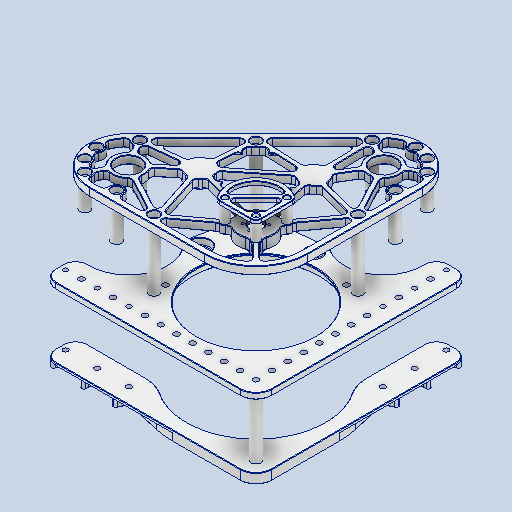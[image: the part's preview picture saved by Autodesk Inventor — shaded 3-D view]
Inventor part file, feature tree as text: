
AUTODESK INVENTOR PART (.ipt)
format: ipt  version: 2024 (Build 280153000, 153)  size: 1,680,896 bytes
history: native  units: in
note: dims shown in document units (in); Inventor stores cm internally (conversion verified against a paired STEP export)
features: other x14, chamfer x3
ambient origin geometry x8: Origin, YZ Plane, XZ Plane, XY Plane, X Axis, Y Axis, Z Axis, Center Point
bodies: Solid1 (feature_tree), Solid2 (feature_tree), Solid3 (feature_tree), Solid4 (feature_tree), Solid5 (feature_tree), Solid6 (feature_tree), Solid7 (feature_tree), Solid8 (feature_tree), Solid9 (feature_tree), Solid10 (feature_tree), Solid11 (feature_tree), Solid12 (feature_tree), Solid13 (feature_tree), Solid14 (feature_tree), Solid15 (feature_tree), Solid16 (feature_tree), Solid17 (feature_tree)
feature tree (17):
  other  "Boss-Extrude4[1]"
  other  "Boss-Extrude4[2]"
  other  "Boss-Extrude4[3]"
  other  "Boss-Extrude6[1]"
  other  "Boss-Extrude6[4]"
  other  "Boss-Extrude6[5]"
  other  "Boss-Extrude6[8]"
  other  "Boss-Extrude9[1]"
  other  "Boss-Extrude17[1]"
  other  "Boss-Extrude17[2]"
  other  "Boss-Extrude17[3]"
  chamfer  "Chamfer4"  [1 undecoded]
  other  "Move Face1"
  chamfer  "Chamfer1"  [1 undecoded]
  chamfer  "Chamfer2"  [1 undecoded]
  other  "Boss-Extrude6[9]"
  other  "Boss-Extrude6[10]"
note: 3 required parameter values undecoded (feature->parameter linkage not recoverable at this tier; creation-order binding heuristic only, values carry confidence <= 0.55)
